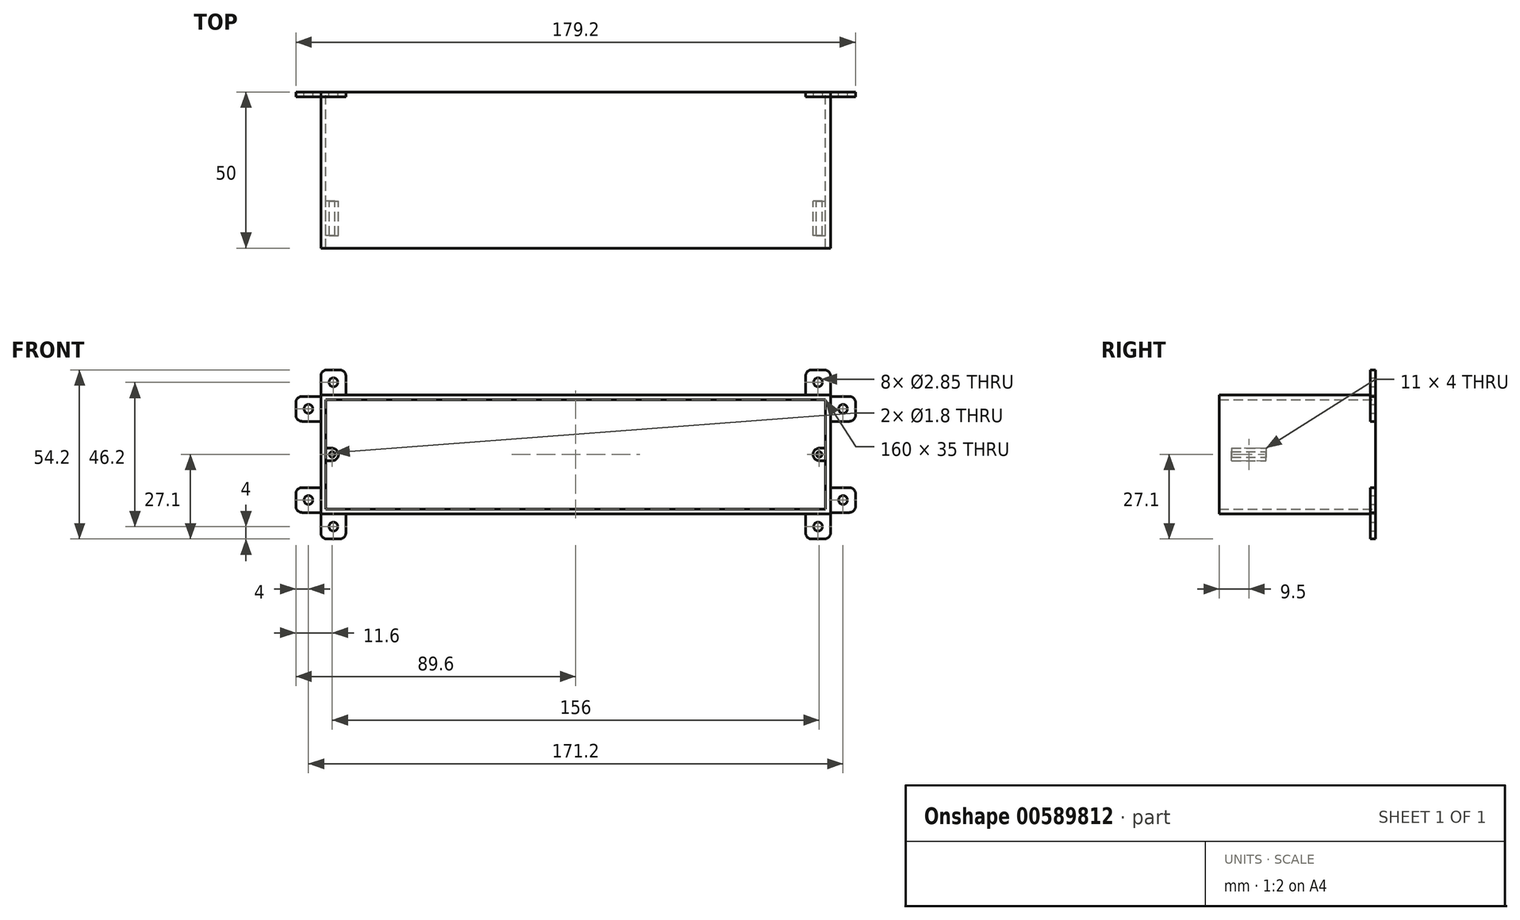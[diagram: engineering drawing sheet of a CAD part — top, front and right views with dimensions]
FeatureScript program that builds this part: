
annotation { "Feature Type Name" : "Feature", "Feature Type Description" : "" }
export const myFeature = defineFeature(function(context is Context, id is Id, definition is map)
    precondition{}
    {
        {
            var Q0;
            Q0=qCreatedBy(makeId("Front.planeOp"),FACE);
            var sketch = newSketch(context, id + "F0", { "sketchPlane" : qUnion([Q0])});
            skLineSegment(sketch, "E0.bottom", {"start": v(80, -17.5) * mm, "end": v(-80, -17.5) * mm});
            skLineSegment(sketch, "E0.top", {"start": v(80, 17.5) * mm, "end": v(-80, 17.5) * mm});
            skLineSegment(sketch, "E0.left", {"start": v(80, -17.5) * mm, "end": v(80, 17.5) * mm});
            skLineSegment(sketch, "E0.right", {"start": v(-80, -17.5) * mm, "end": v(-80, 17.5) * mm});
            skPoint(sketch, "E0.middle", {"position": v(0, 0) * mm});
            skLineSegment(sketch, "E1.0", {"start": v(-81.6, -19.1) * mm, "end": v(-81.6, 19.1) * mm});
            skLineSegment(sketch, "E1.1", {"start": v(81.6, -19.1) * mm, "end": v(-81.6, -19.1) * mm});
            skLineSegment(sketch, "E1.2", {"start": v(81.6, -19.1) * mm, "end": v(81.6, 19.1) * mm});
            skLineSegment(sketch, "E1.3", {"start": v(81.6, 19.1) * mm, "end": v(-81.6, 19.1) * mm});
            skLineSegment(sketch, "E2.bottom", {"start": v(-81.6, 19.1) * mm, "end": v(-73.6, 19.1) * mm});
            skLineSegment(sketch, "E2.top", {"start": v(-81.6, 27.1) * mm, "end": v(-73.6, 27.1) * mm});
            skLineSegment(sketch, "E2.left", {"start": v(-81.6, 19.1) * mm, "end": v(-81.6, 27.1) * mm});
            skLineSegment(sketch, "E2.right", {"start": v(-73.6, 19.1) * mm, "end": v(-73.6, 27.1) * mm});
            skLineSegment(sketch, "E3.bottom", {"start": v(89.6, -18.6) * mm, "end": v(81.6, -18.6) * mm});
            skLineSegment(sketch, "E3.top", {"start": v(89.6, -10.6) * mm, "end": v(81.6, -10.6) * mm});
            skLineSegment(sketch, "E3.left", {"start": v(89.6, -18.6) * mm, "end": v(89.6, -10.6) * mm});
            skPoint(sketch, "E3.middle", {"position": v(81.6, 0) * mm});
            skLineSegment(sketch, "E4.MirrorCS", {"start": v(-81.6, -19.1) * mm, "end": v(-81.6, -27.1) * mm});
            skLineSegment(sketch, "E5.MirrorCS", {"start": v(-81.6, -27.1) * mm, "end": v(-73.6, -27.1) * mm});
            skLineSegment(sketch, "E6.MirrorCS", {"start": v(-73.6, -19.1) * mm, "end": v(-73.6, -27.1) * mm});
            skLineSegment(sketch, "E7.MirrorCS", {"start": v(-81.6, -19.1) * mm, "end": v(-73.6, -19.1) * mm});
            skLineSegment(sketch, "E8.MirrorCS", {"start": v(73.6, 19.1) * mm, "end": v(73.6, 27.1) * mm});
            skLineSegment(sketch, "E9.MirrorCS", {"start": v(81.6, 27.1) * mm, "end": v(73.6, 27.1) * mm});
            skLineSegment(sketch, "E10.MirrorCS", {"start": v(81.6, 19.1) * mm, "end": v(81.6, 27.1) * mm});
            skLineSegment(sketch, "E11.MirrorCS", {"start": v(81.6, 19.1) * mm, "end": v(73.6, 19.1) * mm});
            skLineSegment(sketch, "E12.MirrorCS", {"start": v(81.6, -19.1) * mm, "end": v(73.6, -19.1) * mm});
            skLineSegment(sketch, "E13.MirrorCS", {"start": v(81.6, -19.1) * mm, "end": v(81.6, -27.1) * mm});
            skLineSegment(sketch, "E14.MirrorCS", {"start": v(81.6, -27.1) * mm, "end": v(73.6, -27.1) * mm});
            skLineSegment(sketch, "E15.MirrorCS", {"start": v(73.6, -19.1) * mm, "end": v(73.6, -27.1) * mm});
            skLineSegment(sketch, "E16.MirrorCS", {"start": v(-89.6, -10.6) * mm, "end": v(-81.6, -10.6) * mm});
            skLineSegment(sketch, "E17.MirrorCS", {"start": v(-89.6, -18.6) * mm, "end": v(-89.6, -10.6) * mm});
            skLineSegment(sketch, "E18.MirrorCS", {"start": v(-89.6, -18.6) * mm, "end": v(-81.6, -18.6) * mm});
            skLineSegment(sketch, "E19", {"start": v(-81.6, 27.1) * mm, "end": v(-73.6, 19.1) * mm, "construction": true});
            skLineSegment(sketch, "E20", {"start": v(-73.6, 27.1) * mm, "end": v(-81.6, 19.1) * mm, "construction": true});
            skCircle(sketch, "E21", {"center": v(-77.6, 23.1) * mm, "radius": 1.43 * mm});
            skCircle(sketch, "E22.MirrorC", {"center": v(77.6, 23.1) * mm, "radius": 1.43 * mm});
            skCircle(sketch, "E23.MirrorC", {"center": v(-77.6, -23.1) * mm, "radius": 1.43 * mm});
            skCircle(sketch, "E24.MirrorC", {"center": v(77.6, -23.1) * mm, "radius": 1.43 * mm});
            skLineSegment(sketch, "E25", {"start": v(-89.6, -10.6) * mm, "end": v(-81.6, -18.6) * mm, "construction": true});
            skLineSegment(sketch, "E26", {"start": v(-89.6, -18.6) * mm, "end": v(-81.6, -10.6) * mm, "construction": true});
            skCircle(sketch, "E27", {"center": v(-85.6, -14.6) * mm, "radius": 1.43 * mm});
            skCircle(sketch, "E28.MirrorC", {"center": v(85.6, -14.6) * mm, "radius": 1.43 * mm});
            skLineSegment(sketch, "E29.top", {"start": v(76, -2) * mm, "end": v(80, -2) * mm});
            skLineSegment(sketch, "E29.left", {"start": v(76, 2) * mm, "end": v(76, -2) * mm});
            skPoint(sketch, "E29.middle", {"position": v(80, 0) * mm});
            skLineSegment(sketch, "E30", {"start": v(76, 2) * mm, "end": v(80, 2) * mm});
            skLineSegment(sketch, "E31", {"start": v(80, 2) * mm, "end": v(76, -2) * mm, "construction": true});
            skLineSegment(sketch, "E32", {"start": v(76, 2) * mm, "end": v(80, -2) * mm, "construction": true});
            skCircle(sketch, "E33", {"center": v(78, 0) * mm, "radius": 0.9 * mm});
            skLineSegment(sketch, "E34.MirrorCS", {"start": v(89.6, 18.6) * mm, "end": v(81.6, 18.6) * mm});
            skLineSegment(sketch, "E35.MirrorCS", {"start": v(89.6, 10.6) * mm, "end": v(81.6, 10.6) * mm});
            skLineSegment(sketch, "E36.MirrorCS", {"start": v(89.6, 18.6) * mm, "end": v(89.6, 10.6) * mm});
            skCircle(sketch, "E37.MirrorC", {"center": v(85.6, 14.6) * mm, "radius": 1.43 * mm});
            skLineSegment(sketch, "E38.MirrorCS", {"start": v(-89.6, 10.6) * mm, "end": v(-81.6, 10.6) * mm});
            skLineSegment(sketch, "E39.MirrorCS", {"start": v(-89.6, 18.6) * mm, "end": v(-89.6, 10.6) * mm});
            skLineSegment(sketch, "E40.MirrorCS", {"start": v(-89.6, 18.6) * mm, "end": v(-81.6, 18.6) * mm});
            skCircle(sketch, "E41.MirrorC", {"center": v(-85.6, 14.6) * mm, "radius": 1.43 * mm});
            skSolve(sketch);
        }
        {
            var Q0;
            Q0=makeQuery(id+"F0.imprint","IMPRINT",FACE,{"disambiguationData":[TD([[makeQuery(id+"F0.imprint","IMPRINT",EDGE,{"derivedFrom":sQuery(id+"F0.wireOp",EDGE,"E0.bottom")}),1.0]])]});
            extrude(context, id + "F1", {"entities" : qUnion([Q0]), "depth" : 50 * mm, "offsetDistance" : 25 * mm});
        }
        {
            var Q0;
            Q0=qSketchRegion(id+"F0",true);
            extrude(context, id + "F2", {"entities" : qUnion([Q0]), "operationType" : NewBodyOperationType.ADD, "depth" : 1.6 * mm, "offsetDistance" : 25 * mm});
        }
        {
            var Q0;
            Q0=makeQuery(id+"F2.opExtrude","SWEPT_EDGE",EDGE,{"disambiguationData":[OSD([sQuery(id+"F0.wireOp",EDGE,"E2.top"),sQuery(id+"F0.wireOp",EDGE,"E2.left")])]});
            var Q1;
            Q1=makeQuery(id+"F2.opExtrude","SWEPT_EDGE",EDGE,{"disambiguationData":[OSD([sQuery(id+"F0.wireOp",EDGE,"E2.top"),sQuery(id+"F0.wireOp",EDGE,"E2.right")])]});
            var Q2;
            Q2=makeQuery(id+"F2.opExtrude","SWEPT_EDGE",EDGE,{"disambiguationData":[OSD([sQuery(id+"F0.wireOp",EDGE,"E8.MirrorCS"),sQuery(id+"F0.wireOp",EDGE,"E9.MirrorCS")])]});
            var Q3;
            Q3=makeQuery(id+"F2.opExtrude","SWEPT_EDGE",EDGE,{"disambiguationData":[OSD([sQuery(id+"F0.wireOp",EDGE,"E9.MirrorCS"),sQuery(id+"F0.wireOp",EDGE,"E10.MirrorCS")])]});
            var Q4;
            Q4=makeQuery(id+"F2.opExtrude","SWEPT_EDGE",EDGE,{"disambiguationData":[OSD([sQuery(id+"F0.wireOp",EDGE,"E3.top"),sQuery(id+"F0.wireOp",EDGE,"E3.left")])]});
            var Q5;
            Q5=makeQuery(id+"F2.opExtrude","SWEPT_EDGE",EDGE,{"disambiguationData":[OSD([sQuery(id+"F0.wireOp",EDGE,"E3.bottom"),sQuery(id+"F0.wireOp",EDGE,"E3.left")])]});
            var Q6;
            Q6=makeQuery(id+"F2.opExtrude","SWEPT_EDGE",EDGE,{"disambiguationData":[OSD([sQuery(id+"F0.wireOp",EDGE,"E13.MirrorCS"),sQuery(id+"F0.wireOp",EDGE,"E14.MirrorCS")])]});
            var Q7;
            Q7=makeQuery(id+"F2.opExtrude","SWEPT_EDGE",EDGE,{"disambiguationData":[OSD([sQuery(id+"F0.wireOp",EDGE,"E14.MirrorCS"),sQuery(id+"F0.wireOp",EDGE,"E15.MirrorCS")])]});
            var Q8;
            Q8=makeQuery(id+"F2.opExtrude","SWEPT_EDGE",EDGE,{"disambiguationData":[OSD([sQuery(id+"F0.wireOp",EDGE,"E17.MirrorCS"),sQuery(id+"F0.wireOp",EDGE,"E18.MirrorCS")])]});
            var Q9;
            Q9=makeQuery(id+"F2.opExtrude","SWEPT_EDGE",EDGE,{"disambiguationData":[OSD([sQuery(id+"F0.wireOp",EDGE,"E16.MirrorCS"),sQuery(id+"F0.wireOp",EDGE,"E17.MirrorCS")])]});
            var Q10;
            Q10=makeQuery(id+"F2.opExtrude","SWEPT_EDGE",EDGE,{"disambiguationData":[OSD([sQuery(id+"F0.wireOp",EDGE,"E4.MirrorCS"),sQuery(id+"F0.wireOp",EDGE,"E5.MirrorCS")])]});
            fillet(context, id + "F3", {"entities" : qUnion([Q0, Q1, Q2, Q3, Q4, Q5, Q6, Q7, Q8, Q9, Q10]), "radius" : 2 * mm, "tangentPropagation" : true, "allowEdgeOverflow" : false});
        }
        {
            var Q0;
            Q0=makeQuery(id+"F1.opExtrude","SWEPT_BODY",BODY,{"disambiguationData":[OSD([sQuery(id+"F0.wireOp",EDGE,"E0.bottom"),sQuery(id+"F0.wireOp",EDGE,"E0.top"),sQuery(id+"F0.wireOp",EDGE,"E0.left"),sQuery(id+"F0.wireOp",EDGE,"E0.right"),sQuery(id+"F0.wireOp",EDGE,"E1.0"),sQuery(id+"F0.wireOp",EDGE,"E1.1"),sQuery(id+"F0.wireOp",EDGE,"E1.2"),sQuery(id+"F0.wireOp",EDGE,"E1.3"),sQuery(id+"F0.wireOp",EDGE,"E2.bottom"),sQuery(id+"F0.wireOp",EDGE,"E7.MirrorCS"),sQuery(id+"F0.wireOp",EDGE,"E11.MirrorCS"),sQuery(id+"F0.wireOp",EDGE,"E12.MirrorCS")])]});
            var Q1;
            Q1=qCreatedBy(makeId("Right.planeOp"),FACE);
            mirror(context, id + "F4", {"operationType" : NewBodyOperationType.ADD, "entities" : qUnion([Q0]), "mirrorPlane" : qUnion([Q1])});
        }
        {
            var Q0;
            Q0=makeQuery(id+"F2.opExtrude","SWEPT_EDGE",EDGE,{"disambiguationData":[OSD([sQuery(id+"F0.wireOp",EDGE,"E5.MirrorCS"),sQuery(id+"F0.wireOp",EDGE,"E6.MirrorCS")])]});
            var Q1;
            Q1=makeQuery(id+"F4.opPattern","COPY",EDGE,{"derivedFrom":makeQuery(id+"F2.opExtrude","SWEPT_EDGE",EDGE,{"disambiguationData":[OSD([sQuery(id+"F0.wireOp",EDGE,"E5.MirrorCS"),sQuery(id+"F0.wireOp",EDGE,"E6.MirrorCS")])]}),"instanceName":"1"});
            fillet(context, id + "F5", {"entities" : qUnion([Q0, Q1]), "radius" : 2 * mm, "tangentPropagation" : true, "allowEdgeOverflow" : false});
        }
        {
            var Q0;
            {var subQ1=sQuery(id+"F0.wireOp",EDGE,"E29.top");Q0=makeQuery(id+"F0.imprint","IMPRINT",FACE,{"disambiguationData":[TD([[makeQuery(id+"F0.imprint","IMPRINT",EDGE,{"derivedFrom":subQ1}),1.0]])]});}
            extrude(context, id + "F6", {"entities" : qUnion([Q0]), "operationType" : NewBodyOperationType.ADD, "depth" : 46 * mm, "hasSecondDirection" : true, "secondDirectionOppositeDirection" : false, "secondDirectionDepth" : 35 * mm, "offsetDistance" : 25 * mm});
        }
        {
            var Q0;
            Q0=makeQuery(id+"F6.opExtrude","SWEPT_EDGE",EDGE,{"disambiguationData":[OSD([sQuery(id+"F0.wireOp",EDGE,"E0.left"),sQuery(id+"F0.wireOp",EDGE,"E29.top")])]});
            var Q1;
            Q1=makeQuery(id+"F6.opExtrude","SWEPT_EDGE",EDGE,{"disambiguationData":[OSD([sQuery(id+"F0.wireOp",EDGE,"E29.top"),sQuery(id+"F0.wireOp",EDGE,"E29.left")])]});
            var Q2;
            Q2=makeQuery(id+"F6.opExtrude","SWEPT_EDGE",EDGE,{"disambiguationData":[OSD([sQuery(id+"F0.wireOp",EDGE,"E29.left"),sQuery(id+"F0.wireOp",EDGE,"E30")])]});
            var Q3;
            Q3=makeQuery(id+"F6.opExtrude","SWEPT_EDGE",EDGE,{"disambiguationData":[OSD([sQuery(id+"F0.wireOp",EDGE,"E0.left"),sQuery(id+"F0.wireOp",EDGE,"E30")])]});
            var Q4;
            Q4=makeQuery(id+"F6.opExtrude","CAP_EDGE",EDGE,{"disambiguationData":[OSD([sQuery(id+"F0.wireOp",EDGE,"E0.left")])],"isStart":true});
            fillet(context, id + "F7", {"entities" : qUnion([Q0, Q1, Q2, Q3, Q4]), "radius" : 2 * mm, "tangentPropagation" : true, "allowEdgeOverflow" : false});
        }
        {
            var Q0;
            Q0=makeQuery(id+"F1.opExtrude","SWEPT_BODY",BODY,{"disambiguationData":[OSD([sQuery(id+"F0.wireOp",EDGE,"E0.bottom"),sQuery(id+"F0.wireOp",EDGE,"E0.top"),sQuery(id+"F0.wireOp",EDGE,"E0.left"),sQuery(id+"F0.wireOp",EDGE,"E0.right"),sQuery(id+"F0.wireOp",EDGE,"E1.0"),sQuery(id+"F0.wireOp",EDGE,"E1.1"),sQuery(id+"F0.wireOp",EDGE,"E1.2"),sQuery(id+"F0.wireOp",EDGE,"E1.3"),sQuery(id+"F0.wireOp",EDGE,"E2.bottom"),sQuery(id+"F0.wireOp",EDGE,"E7.MirrorCS"),sQuery(id+"F0.wireOp",EDGE,"E11.MirrorCS"),sQuery(id+"F0.wireOp",EDGE,"E12.MirrorCS")])]});
            var Q1;
            Q1=qCreatedBy(makeId("Right.planeOp"),FACE);
            mirror(context, id + "F8", {"operationType" : NewBodyOperationType.ADD, "entities" : qUnion([Q0]), "mirrorPlane" : qUnion([Q1])});
        }
        {
            var Q0;
            Q0=makeQuery(id+"F2.opExtrude","SWEPT_EDGE",EDGE,{"disambiguationData":[OSD([sQuery(id+"F0.wireOp",EDGE,"E35.MirrorCS"),sQuery(id+"F0.wireOp",EDGE,"E36.MirrorCS")])]});
            var Q1;
            Q1=makeQuery(id+"F2.opExtrude","SWEPT_EDGE",EDGE,{"disambiguationData":[OSD([sQuery(id+"F0.wireOp",EDGE,"E34.MirrorCS"),sQuery(id+"F0.wireOp",EDGE,"E36.MirrorCS")])]});
            var Q2;
            Q2=makeQuery(id+"F2.opExtrude","SWEPT_EDGE",EDGE,{"disambiguationData":[OSD([sQuery(id+"F0.wireOp",EDGE,"E38.MirrorCS"),sQuery(id+"F0.wireOp",EDGE,"E39.MirrorCS")])]});
            var Q3;
            Q3=makeQuery(id+"F2.opExtrude","SWEPT_EDGE",EDGE,{"disambiguationData":[OSD([sQuery(id+"F0.wireOp",EDGE,"E39.MirrorCS"),sQuery(id+"F0.wireOp",EDGE,"E40.MirrorCS")])]});
            fillet(context, id + "F9", {"entities" : qUnion([Q0, Q1, Q2, Q3]), "radius" : 2 * mm, "tangentPropagation" : true, "allowEdgeOverflow" : false});
        }
    });
